# Revit family: Quiet-RndTop_RndBase
name_source: partatom
category: Furniture
revit_build: Autodesk Revit 2016 (Build: 20150714_1515(x64)
units: mm (PartAtom-declared; Revit-internal decimal feet)

## family parameters
Always vertical = Yes
Cut with Voids When Loaded = No
OmniClass Number = 23.40.20.14.14.17
OmniClass Title = Stools
Room Calculation Point = No
Shared = No
Work Plane-Based = No

## types (19) — shared parameters
Manufacturer = Bernhardt Design
URL = http://bernhardtdesign.com

## per-type parameters (varying)
| type | Base Width | Catalog | Column Radius | Depth | Height | SKU | Top Radius | Width |
| Quiet - QUS-181 18" rnd top/ rnd base occasional | 14" | QUS-181 | 3/8" | 18" | 18" | QUS-181 | 9" | 18" |
| Quiet - QUS-221 22" rnd top/ rnd base occasional | 17 1/2" | QUS-221 | 3/8" | 22" | 18" | QUS-221 | 11" | 22" |
| Quiet - QUS-301 30" rnd top/ rnd base occasional | 20 7/8" | QUS-301 | 1 1/2" | 30" | 13" | QUS-301 | 15" | 30" |
| Quiet - QUS-361 36" rnd top/ rnd base occasional | 20 7/8" | QUS-361 | 1 1/2" | 36" | 13" | QUS-361 | 18" | 36" |
| Quiet - QUS-421 42" rnd top/ rnd base occasional | 24" | QUS-421 | 1 1/2" | 42" | 13" | QUS-421 | 21" | 42" |
| Quiet - QUS-185 18" rnd top/ rnd base mid | 14" | QUS-185 | 7/16" | 18" | 23 3/4" | QUS-185 | 9" | 18" |
| Quiet - QUS-225 22" rnd top/ rnd base mid | 17 1/2" | QUS-225 | 7/16" | 22" | 23 3/4" | QUS-225 | 11" | 22" |
| Quiet - QUS-305 30" rnd top/ rnd base mid | 20 7/8" | QUS-305 | 1 1/2" | 30" | 23 3/4" | QUS-305 | 15" | 30" |
| Quiet - QUS-365 36" rnd top/ rnd base mid | 20 7/8" | QUS-365 | 1 1/2" | 36" | 23 3/4" | QUS-365 | 18" | 36" |
| Quiet - QUS-425 42" rnd top/ rnd base mid | 24" | QUS-425 | 1 1/2" | 42" | 23 3/4" | QUS-425 | 21" | 42" |
| Quiet - QUS-309 30" rnd top/ rnd base conference | 20 7/8" | QUS-309 | 1 1/2" | 30" | 29" | QUS-309 | 15" | 30" |
| Quiet - QUS-369 36" rnd top/ rnd base conference | 20 7/8" | QUS-369 | 1 1/2" | 36" | 29" | QUS-369 | 18" | 36" |
| Quiet - QUS-429 42" rnd top/ rnd base conference | 24" | QUS-429 | 1 1/2" | 42" | 29" | QUS-429 | 21" | 42" |
| Quiet - QUS-271 27" rnd top/ rnd base bar | 20 7/8" | QUS-271 | 1 1/2" | 27" | 42" | QUS-271 | 13 1/2" | 27" |
| Quiet - QUS-485 48" rnd top/ rnd base mid | 24" | QUS-485 | 1 1/2" | 48" | 23 3/4" | QUS-485 | 24" | 48" |
| Quiet - QUS-481 48" rnd top/ rnd base occasional | 24" | QUS-481 | 1 1/2" | 48" | 13" | QUS-481 | 24" | 48" |
| Quiet - QUS-487 48" rnd top/ rnd base conference | 24" | QUS-487 | 1 1/2" | 48" | 29" | QUS-487 | 24" | 48" |
| Quiet - QUS-313 30" rnd top/ rnd base bar | 20 7/8" | QUS-313 | 1 1/2" | 30" | 42" | QUS-313 | 15" | 30" |
| Quiet - QUS-167 16" rnd top/ rnd base occasional | 16" | QUS-167 | 3/8" | 16" | 18" | QUS-167 | 8" | 16" |

## geometry (parser evidence)
native form markers: Blend x8, Sweep x2
no freeform markers — native parametric forms only
